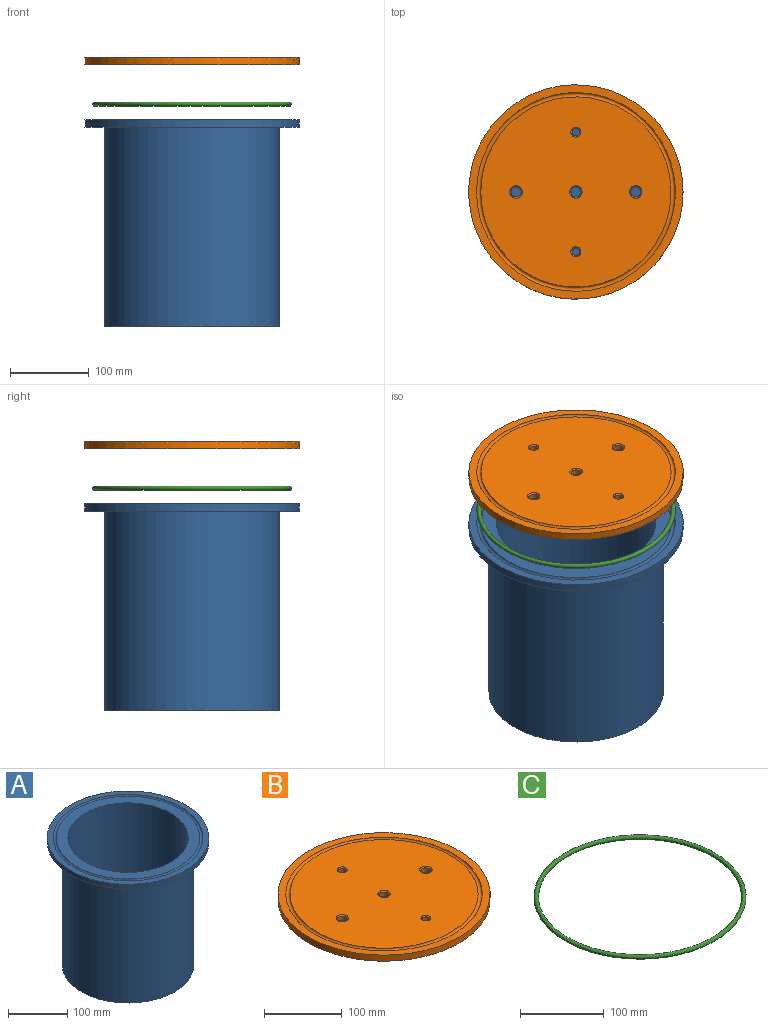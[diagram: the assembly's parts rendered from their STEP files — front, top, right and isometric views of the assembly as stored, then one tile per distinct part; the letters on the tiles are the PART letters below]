
ASSEMBLY  parts=3 mates=2
PART A: 9 faces, bbox 273.9x273.9x265.4 mm
  f0: plane 273.05x273.05mm, normal (0,0,1), area 8270mm2, adj f1,f5
  f1: cylinder r=136.53mm len=273.05mm, axis (0,0,1), area 8170.7mm2, adj f0,f2
  f2: plane 273.05x273.05mm, normal (0,0,-1), area 19761.6mm2, adj f1,f3
  f3: cylinder r=111.12mm len=254mm, axis (0,0,1), area 177347.6mm2, adj f2,f4
  f4: plane 222.25x222.25mm, normal (0,0,-1), area 38794.8mm2, adj f3
  f5: torus R=123.83mm, axis (0,0,1), area 6580.8mm2, adj f0,f8
  f6: plane 203.2x203.2mm, normal (0,0,1), area 32429.3mm2, adj f7
  f7: cylinder r=101.6mm len=254mm, axis (0,0,1), area 162146.4mm2, adj f6,f8
  f8: plane 242.27x242.27mm, normal (0,0,1), area 13667.6mm2, adj f5,f7
PART B: 20 faces, bbox 273.9x273.9x11.4 mm
  f0: plane 242.27x242.27mm, normal (0,0,1), area 45249.8mm2, adj f9,f11,f13,f15,f17,f19
  f1: cylinder r=6.35mm len=12.7mm, axis (0,0,1), area 253.4mm2, adj f14,f15
  f2: cylinder r=6.35mm len=12.7mm, axis (0,0,1), area 253.4mm2, adj f16,f17
  f3: cylinder r=6.35mm len=12.7mm, axis (0,0,1), area 253.4mm2, adj f12,f13
  f4: cylinder r=4.76mm len=9.53mm, axis (0,0,1), area 190mm2, adj f18,f19
  f5: cylinder r=4.76mm len=9.53mm, axis (0,0,1), area 190mm2, adj f10,f11
  f6: cylinder r=136.53mm len=273.05mm, axis (0,0,1), area 8170.7mm2, adj f7,f8
  f7: plane 273.05x273.05mm, normal (0,0,-1), area 57709.2mm2, adj f6,f10,f12,f14,f16,f18
  f8: plane 273.05x273.05mm, normal (0,0,1), area 8270mm2, adj f6,f9
  f9: torus R=123.83mm, axis (0,0,1), area 6580.8mm2, adj f0,f8
  f10: cone r=6.35mm half-angle=45deg, axis (0,0,-1), area 78.4mm2, adj f5,f7
  f11: cone r=4.76mm half-angle=45deg, axis (0,0,1), area 78.4mm2, adj f0,f5
  f12: cone r=7.94mm half-angle=45deg, axis (0,0,-1), area 100.8mm2, adj f3,f7
  f13: cone r=6.35mm half-angle=45deg, axis (0,0,1), area 100.8mm2, adj f0,f3
  f14: cone r=7.94mm half-angle=45deg, axis (0,0,-1), area 100.8mm2, adj f1,f7
  f15: cone r=6.35mm half-angle=45deg, axis (0,0,1), area 100.8mm2, adj f0,f1
  f16: cone r=7.94mm half-angle=45deg, axis (0,0,-1), area 100.8mm2, adj f2,f7
  f17: cone r=6.35mm half-angle=45deg, axis (0,0,1), area 100.8mm2, adj f0,f2
  f18: cone r=6.35mm half-angle=45deg, axis (0,0,-1), area 78.4mm2, adj f4,f7
  f19: cone r=4.76mm half-angle=45deg, axis (0,0,1), area 78.4mm2, adj f0,f4
PART C: 1 faces, bbox 273.9x273.9x5.4 mm
  f0: torus R=123.83mm, axis (0,0,1), area 13161.6mm2
PLACE A t=(56.47,-48.92,-42.05)mm
PLACE B t=(56.47,-48.92,88.98)mm
PLACE C t=(56.47,-48.92,29.39)mm
MATE slider B.f1 <-> C.f0  axis (0,0,1) through (56.47,-48.92,86.28)mm
MATE slider C.f0 <-> A.f1  axis (0,0,1) through (56.47,-48.92,29.39)mm
